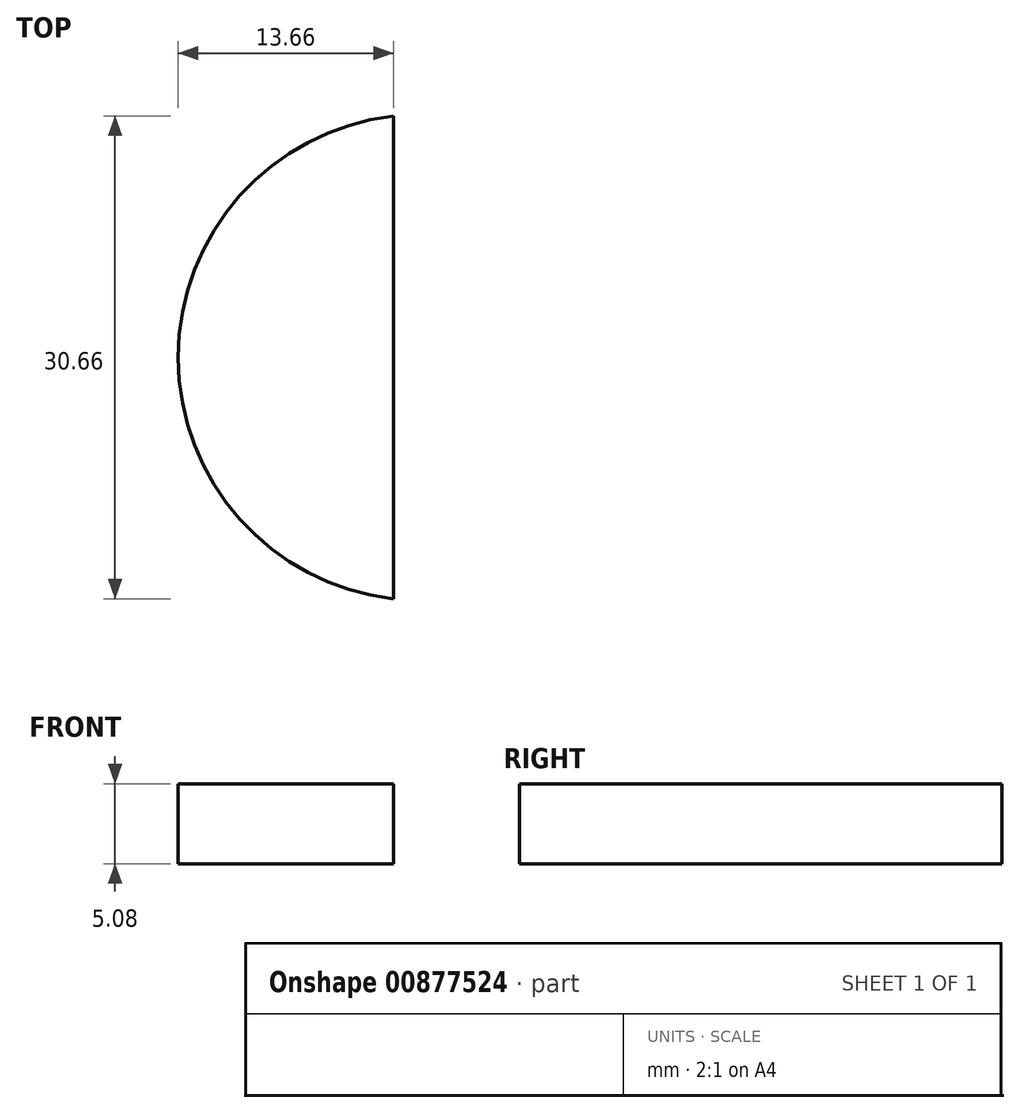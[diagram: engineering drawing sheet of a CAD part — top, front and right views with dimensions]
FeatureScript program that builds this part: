
annotation { "Feature Type Name" : "Feature", "Feature Type Description" : "" }
export const myFeature = defineFeature(function(context is Context, id is Id, definition is map)
    precondition{}
    {
        {
            var Q0;
            Q0=qCreatedBy(makeId("Top.planeOp"),FACE);
            var sketch = newSketch(context, id + "F0", { "sketchPlane" : qUnion([Q0])});
            skArc(sketch, "E0", {"start": v(0, 13.87) * mm, "mid": v(-13.66, -1.46) * mm, "end": v(0, -16.8) * mm});
            skLineSegment(sketch, "E1", {"start": v(0, 13.87) * mm, "end": v(0, -16.8) * mm});
            skSolve(sketch);
        }
        {
            var Q0;
            Q0=makeQuery(id+"F0.imprint","IMPRINT",FACE,{"disambiguationData":[TD([[makeQuery(id+"F0.imprint","IMPRINT",EDGE,{"derivedFrom":sQuery(id+"F0.wireOp",EDGE,"E0")}),1.0]])]});
            extrude(context, id + "F1", {"entities" : qUnion([Q0]), "depth" : 5.08 * mm, "offsetDistance" : 25.4 * mm});
        }
    });
